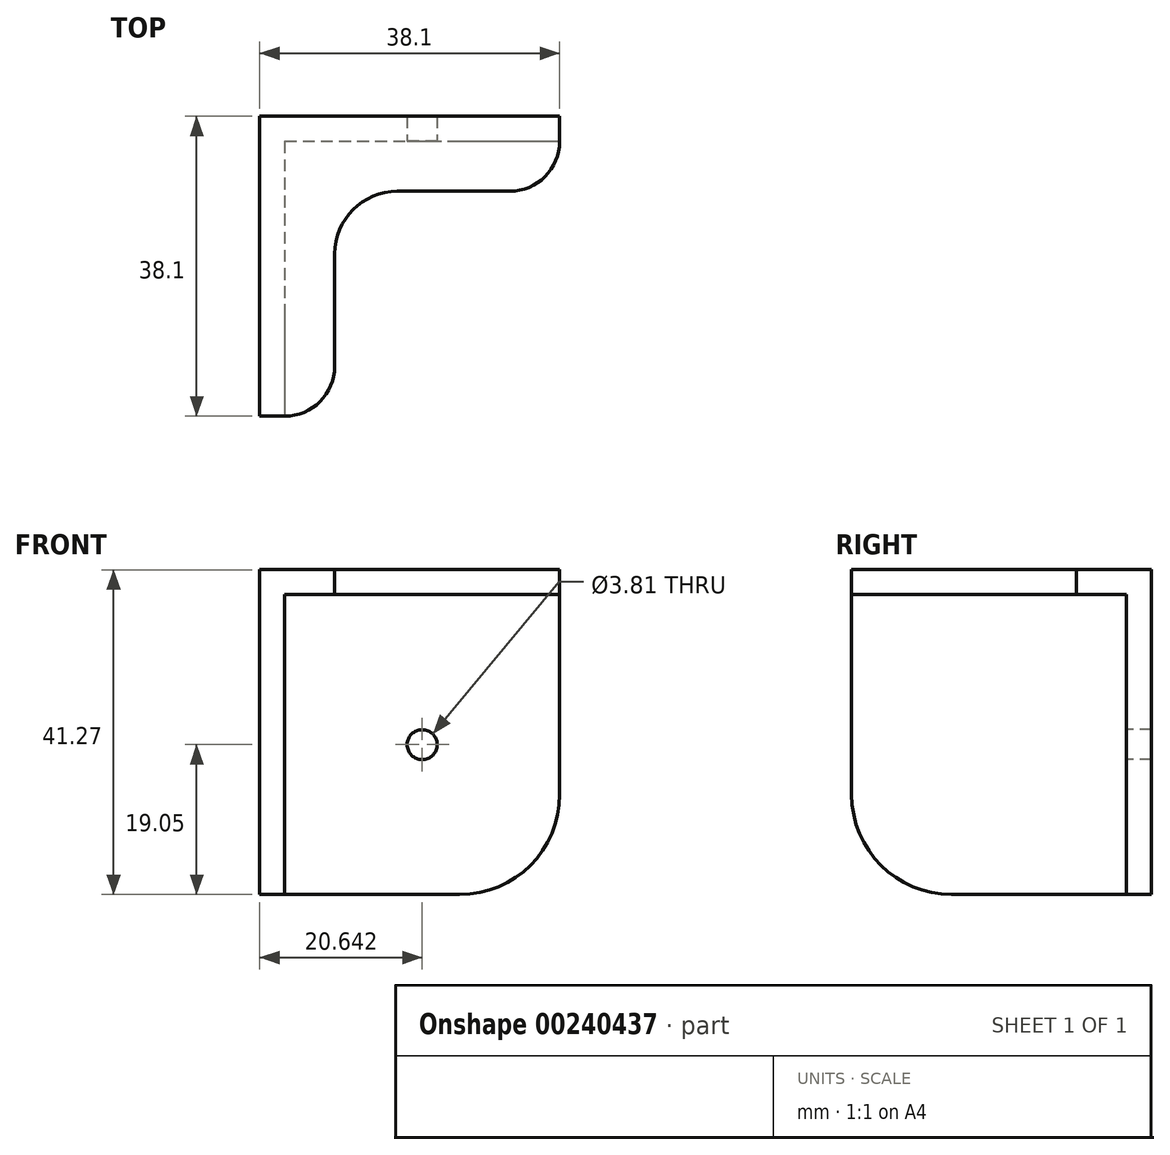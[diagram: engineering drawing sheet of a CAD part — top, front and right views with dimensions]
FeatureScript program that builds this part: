
annotation { "Feature Type Name" : "Feature", "Feature Type Description" : "" }
export const myFeature = defineFeature(function(context is Context, id is Id, definition is map)
    precondition{}
    {
        {
            var Q0;
            Q0=qCreatedBy(makeId("Top.planeOp"),FACE);
            var sketch = newSketch(context, id + "F0", { "sketchPlane" : qUnion([Q0])});
            skLineSegment(sketch, "E0", {"start": v(0, 0) * mm, "end": v(0, -34.92) * mm});
            skLineSegment(sketch, "E1", {"start": v(0, -34.92) * mm, "end": v(-3.17, -34.92) * mm});
            skLineSegment(sketch, "E2", {"start": v(-3.17, -34.92) * mm, "end": v(-3.17, 3.17) * mm});
            skLineSegment(sketch, "E3", {"start": v(-3.17, 3.17) * mm, "end": v(0, 0) * mm, "construction": true});
            skLineSegment(sketch, "E4.MirrorCS", {"start": v(34.92, 3.18) * mm, "end": v(-3.17, 3.17) * mm});
            skLineSegment(sketch, "E5.MirrorCS", {"start": v(0, 0) * mm, "end": v(34.92, 0) * mm});
            skLineSegment(sketch, "E6.MirrorCS", {"start": v(34.92, 0) * mm, "end": v(34.92, 3.18) * mm});
            skSolve(sketch);
        }
        {
            var Q0;
            Q0 = qSketchRegion(id + "F0", true);
            extrude(context, id + "F1", {"entities" : qUnion([Q0]), "oppositeDirection" : true, "depth" : 38.1 * mm});
        }
        {
            var Q0;
            Q0=makeQuery(id+"F1.opExtrude","CAP_FACE",FACE,{"disambiguationData":[OSD([sQuery(id+"F0.wireOp",EDGE,"E0"),sQuery(id+"F0.wireOp",EDGE,"E1"),sQuery(id+"F0.wireOp",EDGE,"E2"),sQuery(id+"F0.wireOp",EDGE,"E4.MirrorCS"),sQuery(id+"F0.wireOp",EDGE,"E5.MirrorCS"),sQuery(id+"F0.wireOp",EDGE,"E6.MirrorCS")])],"isStart":true});
            var sketch = newSketch(context, id + "F2", { "sketchPlane" : qUnion([Q0])});
            skLineSegment(sketch, "E7.0", {"start": v(6.35, -6.35) * mm, "end": v(6.35, -34.92) * mm});
            skLineSegment(sketch, "E7.1", {"start": v(6.35, -6.35) * mm, "end": v(34.92, -6.35) * mm});
            skLineSegment(sketch, "E8", {"start": v(6.35, -34.92) * mm, "end": v(-3.17, -34.92) * mm});
            skLineSegment(sketch, "E9", {"start": v(-3.17, -34.92) * mm, "end": v(-3.17, 3.17) * mm});
            skLineSegment(sketch, "E10", {"start": v(-3.18, 3.17) * mm, "end": v(34.92, 3.18) * mm});
            skLineSegment(sketch, "E11", {"start": v(34.92, 3.18) * mm, "end": v(34.92, -6.35) * mm});
            skSolve(sketch);
        }
        {
            var Q0;
            Q0 = qSketchRegion(id + "F2", true);
            extrude(context, id + "F3", {"entities" : qUnion([Q0]), "operationType" : NewBodyOperationType.ADD, "depth" : 3.17 * mm});
        }
        {
            var Q0;
            Q0=makeQuery(id+"F3.opExtrude","SWEPT_EDGE",EDGE,{"disambiguationData":[OSD([sQuery(id+"F2.wireOp",EDGE,"E7.0"),sQuery(id+"F2.wireOp",EDGE,"E7.1")])]});
            fillet(context, id + "F4", {"entities" : qUnion([Q0]), "radius" : 7.94 * mm, "tangentPropagation" : true, "allowEdgeOverflow" : false});
        }
        {
            var Q0;
            Q0=makeQuery(id+"F3.opExtrude","SWEPT_EDGE",EDGE,{"disambiguationData":[OSD([sQuery(id+"F2.wireOp",EDGE,"E7.0"),sQuery(id+"F2.wireOp",EDGE,"E8")])]});
            var Q1;
            Q1=makeQuery(id+"F3.opExtrude","SWEPT_EDGE",EDGE,{"disambiguationData":[OSD([sQuery(id+"F2.wireOp",EDGE,"E7.1"),sQuery(id+"F2.wireOp",EDGE,"E11")])]});
            fillet(context, id + "F5", {"entities" : qUnion([Q0, Q1]), "radius" : 6.35 * mm, "tangentPropagation" : true, "allowEdgeOverflow" : false});
        }
        {
            var Q0;
            {var subQ0=sQuery(id+"F2.wireOp",EDGE,"E7.1");var subQ1=sQuery(id+"F2.wireOp",EDGE,"E7.0");Q0=makeQuery(id+"F4.opFillet","BLEND_EDGE",EDGE,{"blendedFrom":[makeQuery(id+"F3.opExtrude","SWEPT_EDGE",EDGE,{"disambiguationData":[OSD([subQ1,subQ0])]}),makeQuery(id+"F3.opExtrude","CAP_FACE",FACE,{"disambiguationData":[OSD([subQ1,subQ0,sQuery(id+"F2.wireOp",EDGE,"E8"),sQuery(id+"F2.wireOp",EDGE,"E9"),sQuery(id+"F2.wireOp",EDGE,"E10"),sQuery(id+"F2.wireOp",EDGE,"E11")])],"isStart":false})],"blendedInto":[makeQuery(id+"F3.opExtrude","CAP_FACE",FACE,{"disambiguationData":[OSD([subQ1,subQ0,sQuery(id+"F2.wireOp",EDGE,"E8"),sQuery(id+"F2.wireOp",EDGE,"E9"),sQuery(id+"F2.wireOp",EDGE,"E10"),sQuery(id+"F2.wireOp",EDGE,"E11")])],"isStart":false})]});}
            cPoint(context, id + "F6", {"entities" : qUnion([Q0]), "parameter" : 0.5});
        }
        {
            var Q0;
            Q0=makeQuery(id+"F1.opExtrude","SWEPT_EDGE",EDGE,{"disambiguationData":[OSD([sQuery(id+"F0.wireOp",EDGE,"E0"),sQuery(id+"F0.wireOp",EDGE,"E5.MirrorCS")])]});
            cPoint(context, id + "F7", {"entities" : qUnion([Q0]), "parameter" : 0.5});
        }
        {
            var Q0;
            Q0 = qCreatedBy(id + "F6" ,VERTEX);
            var Q1;
            Q1=makeQuery(id+"F1.opExtrude","CAP_VERTEX",VERTEX,{"disambiguationData":[OSD([sQuery(id+"F0.wireOp",EDGE,"E0"),sQuery(id+"F0.wireOp",EDGE,"E5.MirrorCS")])],"isStart":false});
            var Q2;
            Q2 = qCreatedBy(id + "F7" ,VERTEX);
            cPlane(context, id + "F8", {"entities" : qUnion([Q0, Q1, Q2]), "cplaneType" : CPlaneType.THREE_POINT, "offset" : 25.4 * mm, "width" : 152.4 * mm, "height" : 152.4 * mm});
        }
        {
            var Q0;
            Q0=makeQuery(id+"F1.opExtrude","CAP_EDGE",EDGE,{"disambiguationData":[OSD([sQuery(id+"F0.wireOp",EDGE,"E6.MirrorCS")])],"isStart":false});
            var Q1;
            Q1=makeQuery(id+"F1.opExtrude","CAP_EDGE",EDGE,{"disambiguationData":[OSD([sQuery(id+"F0.wireOp",EDGE,"E1")])],"isStart":false});
            fillet(context, id + "F9", {"entities" : qUnion([Q0, Q1]), "radius" : 12.7 * mm, "tangentPropagation" : true, "allowEdgeOverflow" : false});
        }
        {
            var Q0;
            Q0=makeQuery(id+"F1.opExtrude","SWEPT_FACE",FACE,{"disambiguationData":[OSD([sQuery(id+"F0.wireOp",EDGE,"E5.MirrorCS")])]});
            var sketch = newSketch(context, id + "F10", { "sketchPlane" : qUnion([Q0])});
            skCircle(sketch, "E12", {"center": v(17.46, -19.05) * mm, "radius": 1.9 * mm});
            skSolve(sketch);
        }
        {
            var Q0;
            Q0 = qSketchRegion(id + "F10", true);
            extrude(context, id + "F11", {"entities" : qUnion([Q0]), "operationType" : NewBodyOperationType.REMOVE, "endBound" : BoundingType.THROUGH_ALL, "oppositeDirection" : true, "depth" : 25.4 * mm});
        }
    });
